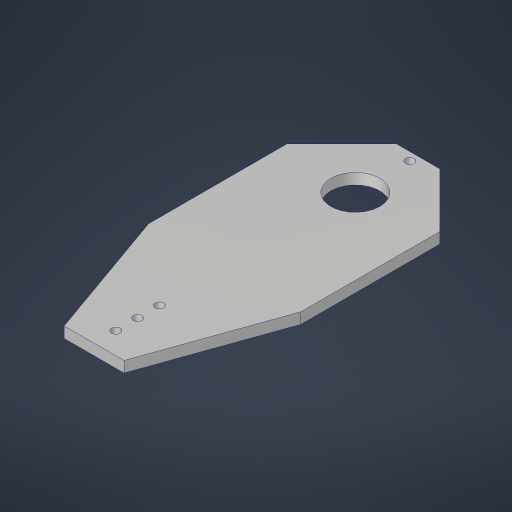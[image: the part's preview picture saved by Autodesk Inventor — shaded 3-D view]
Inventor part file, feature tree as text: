
AUTODESK INVENTOR PART (.ipt)
format: ipt  version: 2023.4 (Build 274418000, 418)  size: 205,312 bytes
history: native  units: in
note: dims shown in document units (in); Inventor stores cm internally (conversion verified against a paired STEP export)
features: sketch x3, extrude x2, hole x2, projected_geometry x1
ambient origin geometry x8: Origin, YZ Plane, XZ Plane, XY Plane, X Axis, Y Axis, Z Axis, Center Point
bodies: Solid1 (feature_tree)
feature tree (8):
  sketch  "Sketch1"  dims[d0=2.0in d1=1.0in]
  extrude  "Extrusion1"  Depth=1.0in
  hole  "Hole1"  [1 undecoded]
  extrude  "Extrusion2"  Depth=0.25in
  hole  "Hole2"  [1 undecoded]
  sketch  "Sketch2"  dims[d2=3.5in d4=1.125in]
  sketch  "Sketch3"  dims[d5=0.375in d6=1.25in d7=6.0in d8=0.25in d9=0.0in d11=0.201in d12=0.75in d13=0.385in d14=0.25in d15=0.5635in d16=1.0in d17=0.8108in d18=1.0in d19=1.25in d20=1.25in d21=1.0in d22=2.0in d23=1.375in d24=3.0in d25=0.0in d26=0.0in d27=0.5in d28=1.0in d29=0.201in d30=0.38in d31=0.385in d32=0.25in d33=0.5635in d34=1.0in d35=0.8108in]
  projected_geometry  "Project Cut Edges1"
note: 2 required parameter values undecoded (feature->parameter linkage not recoverable at this tier; creation-order binding heuristic only, values carry confidence <= 0.55)
